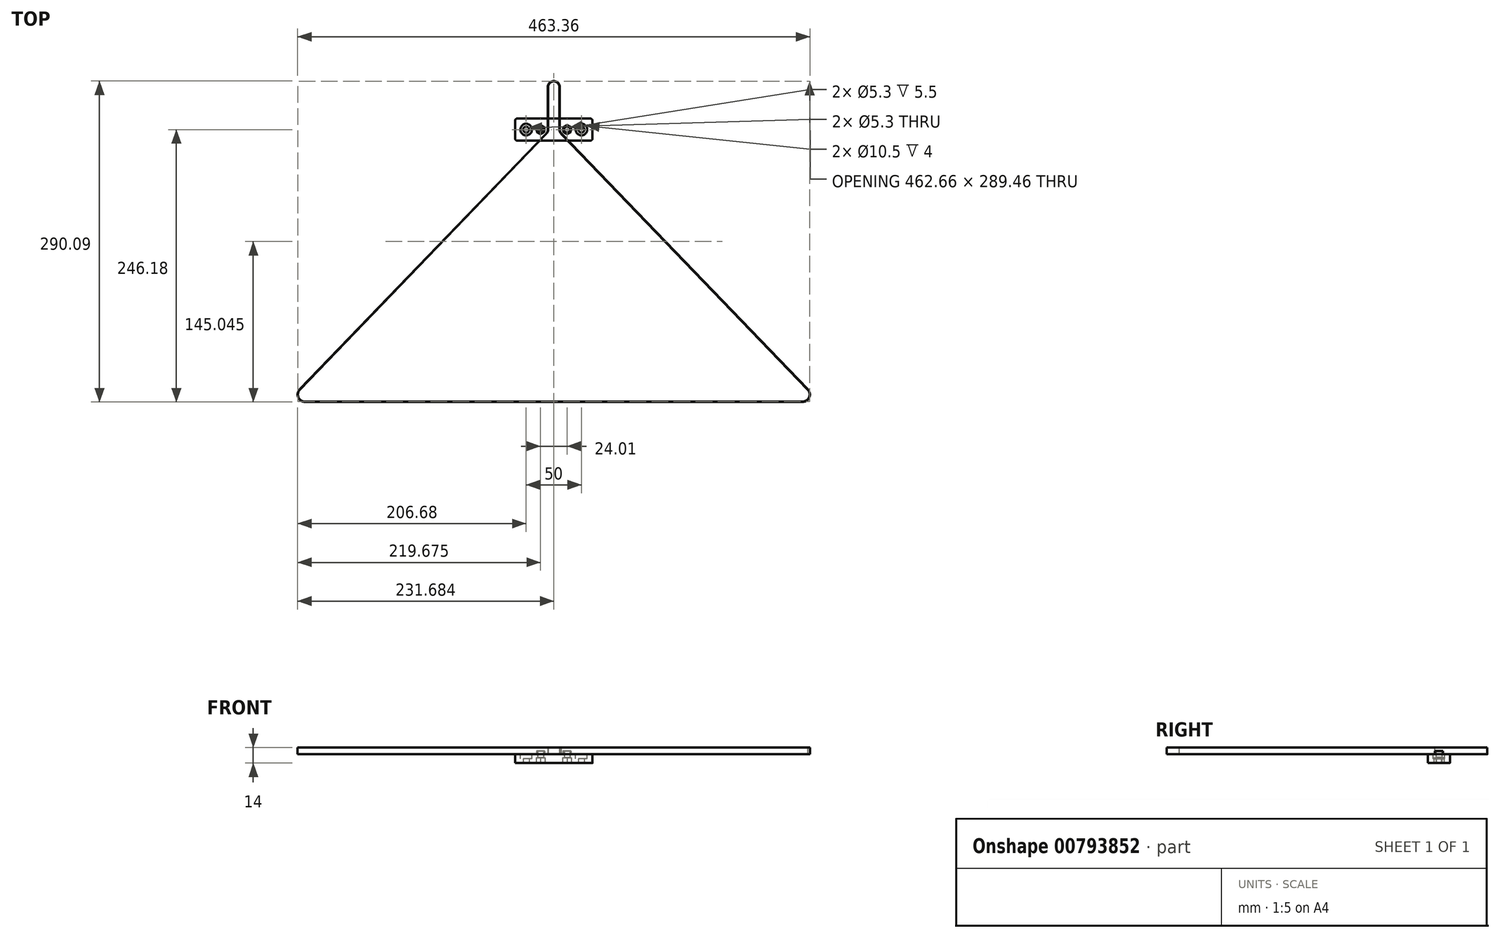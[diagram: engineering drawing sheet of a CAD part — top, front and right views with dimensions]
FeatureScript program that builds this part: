
annotation { "Feature Type Name" : "Feature", "Feature Type Description" : "" }
export const myFeature = defineFeature(function(context is Context, id is Id, definition is map)
    precondition{}
    {
        {
            var Q0;
            Q0=qCreatedBy(makeId("Top.planeOp"),FACE);
            var sketch = newSketch(context, id + "F0", { "sketchPlane" : qUnion([Q0])});
            skLineSegment(sketch, "E0", {"start": v(-225, 0) * mm, "end": v(225, 0) * mm, "construction": true});
            skLineSegment(sketch, "E1", {"start": v(225, 0) * mm, "end": v(0, 278) * mm, "construction": true});
            skLineSegment(sketch, "E2", {"start": v(0, 278) * mm, "end": v(-225, 0) * mm, "construction": true});
            skArc(sketch, "E3", {"start": v(-221, 4.95) * mm, "mid": v(-231, 2.12) * mm, "end": v(-225, -6.36) * mm});
            skArc(sketch, "E4", {"start": v(225, -6.37) * mm, "mid": v(230.88, -2.43) * mm, "end": v(229.5, 4.5) * mm});
            skLineSegment(sketch, "E5", {"start": v(-5.1, 279.81) * mm, "end": v(-5.1, 279.8) * mm});
            skLineSegment(sketch, "E6", {"start": v(5.1, 279.81) * mm, "end": v(5.1, 279.8) * mm});
            skLineSegment(sketch, "E7", {"start": v(225, -6.36) * mm, "end": v(-225, -6.37) * mm});
            skPoint(sketch, "E8.orphan", {"position": v(0, 286.06) * mm});
            skPoint(sketch, "E9.orphan", {"position": v(233.21, 0) * mm});
            skArc(sketch, "E10", {"start": v(-220.8, 5.2) * mm, "mid": v(-231.3, 2.23) * mm, "end": v(-225, -6.68) * mm});
            skArc(sketch, "E11", {"start": v(225, -6.68) * mm, "mid": v(231.15, -2.61) * mm, "end": v(229.8, 4.64) * mm});
            skLineSegment(sketch, "E12", {"start": v(-225, -6.68) * mm, "end": v(225, -6.68) * mm});
            skLineSegment(sketch, "E13.trimOffspring", {"start": v(0, 298.25) * mm, "end": v(0.15, 298.42) * mm});
            skPoint(sketch, "E14.orphan", {"position": v(243.86, 0) * mm});
            skArc(sketch, "E15", {"start": v(-6.84, 235.96) * mm, "mid": v(-5.78, 237.6) * mm, "end": v(-5.4, 239.5) * mm});
            skArc(sketch, "E16", {"start": v(5.41, 239.5) * mm, "mid": v(5.78, 237.6) * mm, "end": v(6.84, 235.96) * mm});
            skArc(sketch, "E17.converted", {"start": v(5.4, 278) * mm, "mid": v(0, 283.41) * mm, "end": v(-5.4, 278) * mm});
            skArc(sketch, "E18.converted", {"start": v(5.1, 278) * mm, "mid": v(0, 283.1) * mm, "end": v(-5.1, 278) * mm});
            skArc(sketch, "E19", {"start": v(-6.6, 235.75) * mm, "mid": v(-5.49, 237.48) * mm, "end": v(-5.1, 239.5) * mm});
            skArc(sketch, "E20", {"start": v(5.1, 239.5) * mm, "mid": v(5.5, 237.42) * mm, "end": v(6.69, 235.67) * mm});
            skLineSegment(sketch, "E21", {"start": v(-5.1, 279.82) * mm, "end": v(-5.1, 279.81) * mm});
            skLineSegment(sketch, "E22", {"start": v(5.1, 279.82) * mm, "end": v(5.1, 279.81) * mm});
            skLineSegment(sketch, "E23", {"start": v(5.4, 278) * mm, "end": v(5.41, 239.5) * mm});
            skLineSegment(sketch, "E24.trimOffspring", {"start": v(-5.4, 278) * mm, "end": v(-5.4, 239.5) * mm});
            skLineSegment(sketch, "E25.trimOffspring", {"start": v(-5.1, 278) * mm, "end": v(-5.1, 239.5) * mm});
            skLineSegment(sketch, "E26.trimOffspring", {"start": v(5.1, 278) * mm, "end": v(5.1, 239.5) * mm});
            skPoint(sketch, "E27.orphan", {"position": v(4.09, 281.55) * mm});
            skPoint(sketch, "E28.orphan", {"position": v(5.1, 281.55) * mm});
            skLineSegment(sketch, "E29", {"start": v(-229.8, 4.64) * mm, "end": v(-6.84, 235.96) * mm});
            skPoint(sketch, "E30.orphan", {"position": v(-234.28, 0) * mm});
            skLineSegment(sketch, "E31", {"start": v(-234.28, -0.45) * mm, "end": v(-6.6, 235.75) * mm});
            skLineSegment(sketch, "E32", {"start": v(6.84, 235.96) * mm, "end": v(229.8, 4.64) * mm});
            skLineSegment(sketch, "E33.trimOffspring", {"start": v(6.69, 235.67) * mm, "end": v(229.5, 4.5) * mm});
            skSolve(sketch);
        }
        {
            var Q0;
            Q0=qSketchRegion(id+"F0",true);
            extrude(context, id + "F1", {"entities" : qUnion([Q0]), "depth" : 6 * mm, "offsetDistance" : 25 * mm});
        }
        {
            var Q0;
            Q0=qCreatedBy(makeId("Top.planeOp"),FACE);
            var sketch = newSketch(context, id + "F2", { "sketchPlane" : qUnion([Q0])});
            skLineSegment(sketch, "E34.bottom", {"start": v(-35, 249.5) * mm, "end": v(35, 249.5) * mm});
            skLineSegment(sketch, "E34.top", {"start": v(-35, 229.5) * mm, "end": v(35, 229.5) * mm});
            skLineSegment(sketch, "E34.left", {"start": v(-35, 249.5) * mm, "end": v(-35, 229.5) * mm});
            skLineSegment(sketch, "E34.right", {"start": v(35, 249.5) * mm, "end": v(35, 229.5) * mm});
            skArc(sketch, "E35.0", {"start": v(-6.84, 235.96) * mm, "mid": v(-5.78, 237.6) * mm, "end": v(-5.4, 239.5) * mm, "construction": true});
            skArc(sketch, "E36.0", {"start": v(5.41, 239.5) * mm, "mid": v(5.78, 237.6) * mm, "end": v(6.84, 235.96) * mm, "construction": true});
            skCircle(sketch, "E37", {"center": v(12, 239.5) * mm, "radius": 2.65 * mm});
            skCircle(sketch, "E38", {"center": v(-12, 239.5) * mm, "radius": 2.65 * mm});
            skPoint(sketch, "E39", {"position": v(0, 283.12) * mm});
            skPoint(sketch, "E40", {"position": v(0, 249.5) * mm});
            skPoint(sketch, "E41", {"position": v(-35, 239.5) * mm});
            skCircle(sketch, "E42", {"center": v(-25, 239.5) * mm, "radius": 2.65 * mm});
            skCircle(sketch, "E43", {"center": v(25, 239.5) * mm, "radius": 2.65 * mm});
            skSolve(sketch);
        }
        {
            var Q0;
            Q0=qSketchRegion(id+"F2",true);
            extrude(context, id + "F3", {"entities" : qUnion([Q0]), "depth" : 8 * mm, "offsetDistance" : 25 * mm});
        }
        {
            var Q0;
            Q0=makeQuery(id+"F3.opExtrude","CAP_FACE",FACE,{"disambiguationData":[OSD([sQuery(id+"F2.wireOp",EDGE,"E34.bottom"),sQuery(id+"F2.wireOp",EDGE,"E34.top"),sQuery(id+"F2.wireOp",EDGE,"E34.left"),sQuery(id+"F2.wireOp",EDGE,"E34.right"),sQuery(id+"F2.wireOp",EDGE,"E37"),sQuery(id+"F2.wireOp",EDGE,"E38"),sQuery(id+"F2.wireOp",EDGE,"E42"),sQuery(id+"F2.wireOp",EDGE,"E43")])],"isStart":false});
            var sketch = newSketch(context, id + "F4", { "sketchPlane" : qUnion([Q0])});
            skPoint(sketch, "E44", {"position": v(-25, 239.5) * mm});
            skPoint(sketch, "E45", {"position": v(25, 239.5) * mm});
            skCircle(sketch, "E46", {"center": v(-25, 239.5) * mm, "radius": 5.25 * mm});
            skCircle(sketch, "E47", {"center": v(25, 239.5) * mm, "radius": 5.25 * mm});
            skSolve(sketch);
        }
        {
            var Q0;
            Q0=qSketchRegion(id+"F4",true);
            extrude(context, id + "F5", {"entities" : qUnion([Q0]), "operationType" : NewBodyOperationType.REMOVE, "oppositeDirection" : true, "depth" : 4 * mm, "offsetDistance" : 25 * mm});
        }
        {
            var Q0;
            Q0=makeQuery(id+"F3.opExtrude","CAP_FACE",FACE,{"disambiguationData":[OSD([sQuery(id+"F2.wireOp",EDGE,"E34.bottom"),sQuery(id+"F2.wireOp",EDGE,"E34.top"),sQuery(id+"F2.wireOp",EDGE,"E34.left"),sQuery(id+"F2.wireOp",EDGE,"E34.right"),sQuery(id+"F2.wireOp",EDGE,"E37"),sQuery(id+"F2.wireOp",EDGE,"E38"),sQuery(id+"F2.wireOp",EDGE,"E42"),sQuery(id+"F2.wireOp",EDGE,"E43")])],"isStart":false});
            var sketch = newSketch(context, id + "F6", { "sketchPlane" : qUnion([Q0])});
            skCircle(sketch, "E48.0", {"center": v(-12, 239.5) * mm, "radius": 2.65 * mm});
            skCircle(sketch, "E49.0", {"center": v(12, 239.5) * mm, "radius": 2.65 * mm});
            skCircle(sketch, "E50", {"center": v(-12, 239.5) * mm, "radius": 3.65 * mm});
            skCircle(sketch, "E51", {"center": v(12, 239.5) * mm, "radius": 3.65 * mm});
            skSolve(sketch);
        }
        {
            var Q0;
            Q0=qSketchRegion(id+"F6",true);
            extrude(context, id + "F7", {"entities" : qUnion([Q0]), "operationType" : NewBodyOperationType.ADD, "depth" : 2.8 * mm, "offsetDistance" : 25 * mm});
        }
        {
            var Q0;
            Q0=makeQuery(id+"F3.opExtrude","SWEPT_EDGE",EDGE,{"disambiguationData":[OSD([sQuery(id+"F2.wireOp",EDGE,"E34.top"),sQuery(id+"F2.wireOp",EDGE,"E34.left")])]});
            var Q1;
            Q1=makeQuery(id+"F3.opExtrude","SWEPT_EDGE",EDGE,{"disambiguationData":[OSD([sQuery(id+"F2.wireOp",EDGE,"E34.bottom"),sQuery(id+"F2.wireOp",EDGE,"E34.left")])]});
            var Q2;
            Q2=makeQuery(id+"F3.opExtrude","SWEPT_EDGE",EDGE,{"disambiguationData":[OSD([sQuery(id+"F2.wireOp",EDGE,"E34.bottom"),sQuery(id+"F2.wireOp",EDGE,"E34.right")])]});
            var Q3;
            Q3=makeQuery(id+"F3.opExtrude","SWEPT_EDGE",EDGE,{"disambiguationData":[OSD([sQuery(id+"F2.wireOp",EDGE,"E34.top"),sQuery(id+"F2.wireOp",EDGE,"E34.right")])]});
            fillet(context, id + "F8", {"entities" : qUnion([Q0, Q1, Q2, Q3]), "radius" : 2 * mm, "tangentPropagation" : true, "allowEdgeOverflow" : false});
        }
        {
            var Q0;
            Q0=makeQuery(id+"F3.opExtrude","CAP_FACE",FACE,{"disambiguationData":[OSD([sQuery(id+"F2.wireOp",EDGE,"E34.bottom"),sQuery(id+"F2.wireOp",EDGE,"E34.top"),sQuery(id+"F2.wireOp",EDGE,"E34.left"),sQuery(id+"F2.wireOp",EDGE,"E34.right"),sQuery(id+"F2.wireOp",EDGE,"E37"),sQuery(id+"F2.wireOp",EDGE,"E38"),sQuery(id+"F2.wireOp",EDGE,"E42"),sQuery(id+"F2.wireOp",EDGE,"E43")])],"isStart":true});
            var sketch = newSketch(context, id + "F9", { "sketchPlane" : qUnion([Q0])});
            skCircle(sketch, "E52.0", {"center": v(-12, -239.5) * mm, "radius": 2.65 * mm, "construction": true});
            skCircle(sketch, "E53.0", {"center": v(12, -239.5) * mm, "radius": 2.65 * mm, "construction": true});
            skCircle(sketch, "E54.cCircle", {"center": v(-12, -239.5) * mm, "radius": 4 * mm, "construction": true});
            skLineSegment(sketch, "E54.0", {"start": v(-8, -237.2) * mm, "end": v(-8, -241.8) * mm});
            skLineSegment(sketch, "E54.1", {"start": v(-8, -241.8) * mm, "end": v(-12, -244.12) * mm});
            skLineSegment(sketch, "E54.2", {"start": v(-12, -244.12) * mm, "end": v(-16, -241.8) * mm});
            skLineSegment(sketch, "E54.3", {"start": v(-16, -241.8) * mm, "end": v(-16, -237.2) * mm});
            skLineSegment(sketch, "E54.4", {"start": v(-16, -237.2) * mm, "end": v(-12, -234.88) * mm});
            skLineSegment(sketch, "E54.5", {"start": v(-12, -234.88) * mm, "end": v(-8, -237.2) * mm});
            skPoint(sketch, "E54.0.midPoint", {"position": v(-8, -239.5) * mm});
            skCircle(sketch, "E55.cCircle", {"center": v(12, -239.5) * mm, "radius": 4 * mm, "construction": true});
            skLineSegment(sketch, "E55.0", {"start": v(16, -237.2) * mm, "end": v(16, -241.8) * mm});
            skLineSegment(sketch, "E55.1", {"start": v(16, -241.8) * mm, "end": v(12, -244.12) * mm});
            skLineSegment(sketch, "E55.2", {"start": v(12, -244.12) * mm, "end": v(8, -241.8) * mm});
            skLineSegment(sketch, "E55.3", {"start": v(8, -241.8) * mm, "end": v(8, -237.2) * mm});
            skLineSegment(sketch, "E55.4", {"start": v(8, -237.2) * mm, "end": v(12, -234.88) * mm});
            skLineSegment(sketch, "E55.5", {"start": v(12, -234.88) * mm, "end": v(16, -237.2) * mm});
            skPoint(sketch, "E55.0.midPoint", {"position": v(16, -239.5) * mm});
            skSolve(sketch);
        }
        {
            var Q0;
            Q0=qSketchRegion(id+"F9",true);
            extrude(context, id + "F10", {"entities" : qUnion([Q0]), "operationType" : NewBodyOperationType.REMOVE, "oppositeDirection" : true, "depth" : 5 * mm, "offsetDistance" : 25 * mm});
        }
        {
            var Q0;
            Q0=makeQuery(id+"F3.opExtrude","SWEPT_BODY",BODY,{"disambiguationData":[OSD([sQuery(id+"F2.wireOp",EDGE,"E34.bottom"),sQuery(id+"F2.wireOp",EDGE,"E34.top"),sQuery(id+"F2.wireOp",EDGE,"E34.left"),sQuery(id+"F2.wireOp",EDGE,"E34.right"),sQuery(id+"F2.wireOp",EDGE,"E37"),sQuery(id+"F2.wireOp",EDGE,"E38"),sQuery(id+"F2.wireOp",EDGE,"E42"),sQuery(id+"F2.wireOp",EDGE,"E43")])]});
            transform(context, id + "F11", {"entities" : qUnion([Q0]), "transformType" : TransformType.TRANSLATION_3D, "dx" : 0 * mm, "dy" : 0 * mm, "dz" : -8 * mm, "makeCopy" : false});
        }
        {
            var Q0;
            Q0=makeQuery(id+"F10.boolean.opBoolean","COPY",FACE,{"derivedFrom":makeQuery(id+"F10.opExtrude","CAP_FACE",FACE,{"disambiguationData":[OSD([sQuery(id+"F9.wireOp",EDGE,"E55.0"),sQuery(id+"F9.wireOp",EDGE,"E55.1"),sQuery(id+"F9.wireOp",EDGE,"E55.2"),sQuery(id+"F9.wireOp",EDGE,"E55.3"),sQuery(id+"F9.wireOp",EDGE,"E55.4"),sQuery(id+"F9.wireOp",EDGE,"E55.5")])],"isStart":false})});
            var sketch = newSketch(context, id + "F12", { "sketchPlane" : qUnion([Q0])});
            skCircle(sketch, "E56.0", {"center": v(12, -239.5) * mm, "radius": 2.65 * mm});
            skCircle(sketch, "E57.0", {"center": v(-12, -239.5) * mm, "radius": 2.65 * mm});
            skSolve(sketch);
        }
        {
            var Q0;
            Q0=qSketchRegion(id+"F12",true);
            extrude(context, id + "F13", {"entities" : qUnion([Q0]), "operationType" : NewBodyOperationType.ADD, "oppositeDirection" : true, "depth" : 0.3 * mm, "offsetDistance" : 25 * mm});
        }
    });
